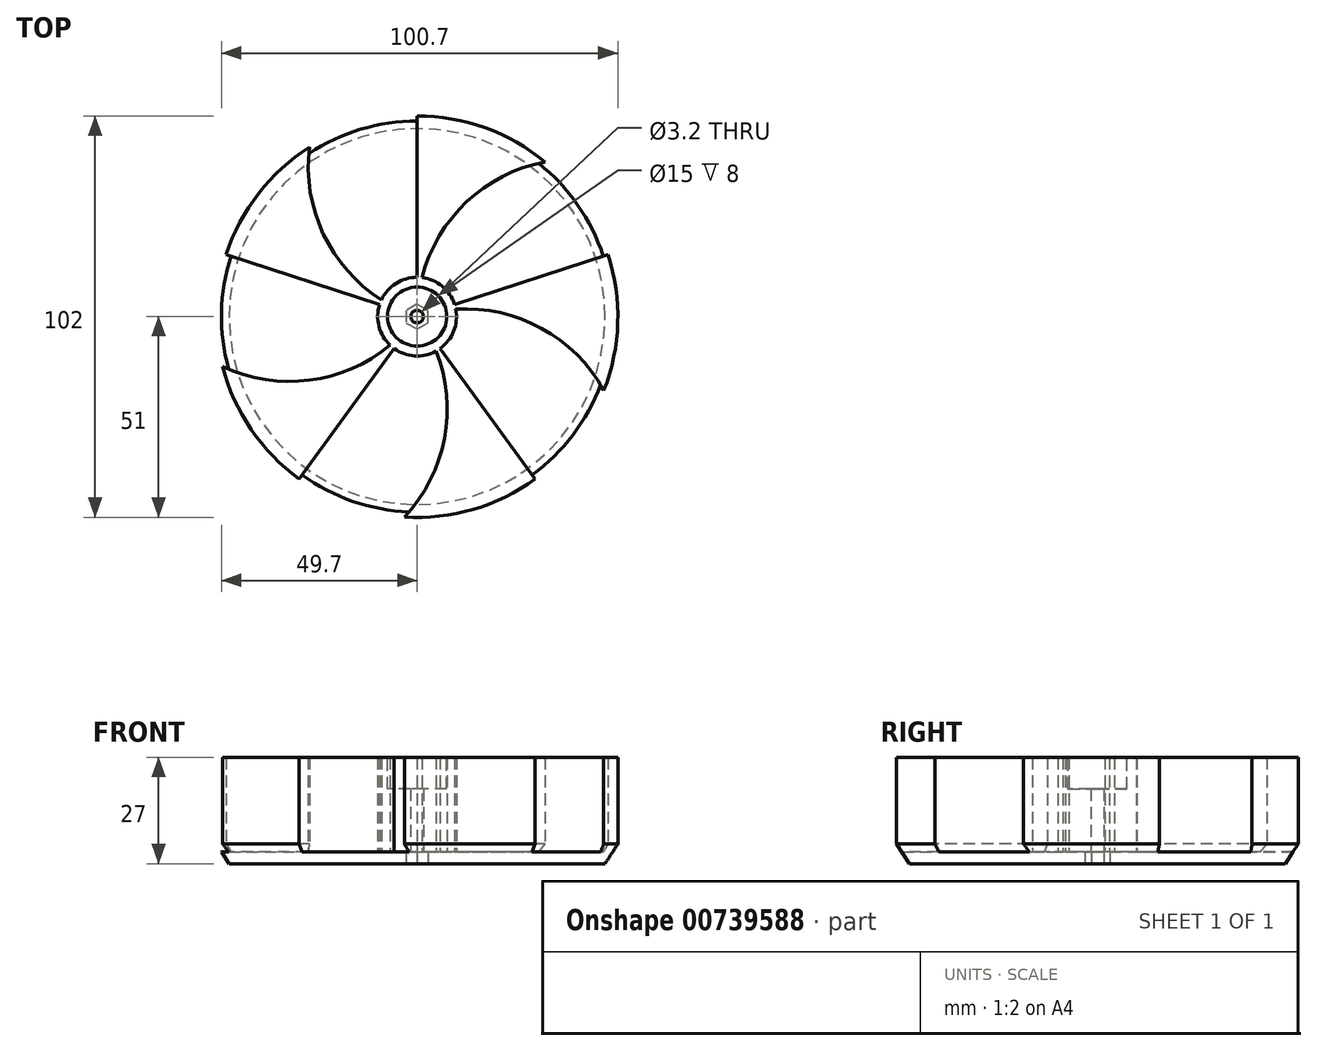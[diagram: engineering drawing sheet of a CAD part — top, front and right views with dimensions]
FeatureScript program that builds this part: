
annotation { "Feature Type Name" : "Feature", "Feature Type Description" : "" }
export const myFeature = defineFeature(function(context is Context, id is Id, definition is map)
    precondition{}
    {
        {
            var Q0;
            Q0=qCreatedBy(makeId("Top.planeOp"),FACE);
            var sketch = newSketch(context, id + "F0", { "sketchPlane" : qUnion([Q0])});
            skCircle(sketch, "E0", {"center": v(0, 0) * mm, "radius": 51 * mm});
            skSolve(sketch);
        }
        {
            var Q0;
            Q0 = qSketchRegion(id + "F0", true);
            extrude(context, id + "F1", {"entities" : qUnion([Q0]), "depth" : 3 * mm, "offsetDistance" : 25 * mm});
        }
        {
            var Q0;
            Q0=makeQuery(id+"F1.opExtrude","CAP_FACE",FACE,{"disambiguationData":[OSD([sQuery(id+"F0.wireOp",EDGE,"E0")])],"isStart":false});
            var sketch = newSketch(context, id + "F2", { "sketchPlane" : qUnion([Q0])});
            skLineSegment(sketch, "E1", {"start": v(0, 0) * mm, "end": v(0, 51) * mm});
            skArc(sketch, "E2", {"start": v(32.51, 39.3) * mm, "mid": v(9.18, 25.5) * mm, "end": v(0, 0) * mm});
            skLineSegment(sketch, "E3.1.0", {"start": v(0, 0) * mm, "end": v(-48.5, 15.76) * mm});
            skArc(sketch, "E3.1.1", {"start": v(-27.32, 43.06) * mm, "mid": v(-21.41, 16.61) * mm, "end": v(0, 0) * mm});
            skLineSegment(sketch, "E3.2.0", {"start": v(0, 0) * mm, "end": v(-29.98, -41.26) * mm});
            skArc(sketch, "E3.2.1", {"start": v(-49.4, -12.68) * mm, "mid": v(-22.42, -15.23) * mm, "end": v(0, 0) * mm});
            skLineSegment(sketch, "E3.3.0", {"start": v(0, 0) * mm, "end": v(29.98, -41.26) * mm});
            skArc(sketch, "E3.3.1", {"start": v(-3.2, -50.9) * mm, "mid": v(7.56, -26.03) * mm, "end": v(0, 0) * mm});
            skLineSegment(sketch, "E3.4.0", {"start": v(0, 0) * mm, "end": v(48.5, 15.76) * mm});
            skArc(sketch, "E3.4.1", {"start": v(47.42, -18.78) * mm, "mid": v(27.09, -0.85) * mm, "end": v(0, 0) * mm});
            skPoint(sketch, "E3.center", {"position": v(0, 0) * mm});
            skCircle(sketch, "E4", {"center": v(0, 0) * mm, "radius": 10 * mm});
            skSolve(sketch);
        }
        {
            var Q0;
            {var subQ0=sQuery(id+"F2.wireOp",EDGE,"E1");var subQ1=makeQuery(id+"F1.opExtrude","CAP_EDGE",EDGE,{"disambiguationData":[OSD([sQuery(id+"F0.wireOp",EDGE,"E0")])],"isStart":false});var subQ2=makeQuery(id+"F2.imprint","INTERSECT",VERTEX,{"derivedFrom":[subQ1,subQ0]});Q0=makeQuery(id+"F2.imprint","IMPRINT",FACE,{"disambiguationData":[TD([[makeQuery(id+"F2.imprint","IMPRINT",EDGE,{"disambiguationData":[TD([[subQ2,1.0]])],"derivedFrom":subQ0}),-1.0]])]});}
            var Q1;
            {var subQ0=sQuery(id+"F2.wireOp",EDGE,"E3.4.0");var subQ1=makeQuery(id+"F1.opExtrude","CAP_EDGE",EDGE,{"disambiguationData":[OSD([sQuery(id+"F0.wireOp",EDGE,"E0")])],"isStart":false});var subQ2=makeQuery(id+"F2.imprint","INTERSECT",VERTEX,{"derivedFrom":[subQ1,subQ0]});Q1=makeQuery(id+"F2.imprint","IMPRINT",FACE,{"disambiguationData":[TD([[makeQuery(id+"F2.imprint","IMPRINT",EDGE,{"disambiguationData":[TD([[subQ2,1.0]])],"derivedFrom":subQ0}),-1.0]])]});}
            var Q2;
            {var subQ0=sQuery(id+"F2.wireOp",EDGE,"E3.3.0");var subQ1=makeQuery(id+"F1.opExtrude","CAP_EDGE",EDGE,{"disambiguationData":[OSD([sQuery(id+"F0.wireOp",EDGE,"E0")])],"isStart":false});var subQ2=makeQuery(id+"F2.imprint","INTERSECT",VERTEX,{"derivedFrom":[subQ1,subQ0]});Q2=makeQuery(id+"F2.imprint","IMPRINT",FACE,{"disambiguationData":[TD([[makeQuery(id+"F2.imprint","IMPRINT",EDGE,{"disambiguationData":[TD([[subQ2,1.0]])],"derivedFrom":subQ0}),-1.0]])]});}
            var Q3;
            {var subQ0=sQuery(id+"F2.wireOp",EDGE,"E3.2.0");var subQ1=makeQuery(id+"F1.opExtrude","CAP_EDGE",EDGE,{"disambiguationData":[OSD([sQuery(id+"F0.wireOp",EDGE,"E0")])],"isStart":false});var subQ2=makeQuery(id+"F2.imprint","INTERSECT",VERTEX,{"derivedFrom":[subQ1,subQ0]});Q3=makeQuery(id+"F2.imprint","IMPRINT",FACE,{"disambiguationData":[TD([[makeQuery(id+"F2.imprint","IMPRINT",EDGE,{"disambiguationData":[TD([[subQ2,1.0]])],"derivedFrom":subQ0}),-1.0]])]});}
            var Q4;
            {var subQ0=sQuery(id+"F2.wireOp",EDGE,"E3.1.0");var subQ1=makeQuery(id+"F1.opExtrude","CAP_EDGE",EDGE,{"disambiguationData":[OSD([sQuery(id+"F0.wireOp",EDGE,"E0")])],"isStart":false});var subQ2=makeQuery(id+"F2.imprint","INTERSECT",VERTEX,{"derivedFrom":[subQ1,subQ0]});Q4=makeQuery(id+"F2.imprint","IMPRINT",FACE,{"disambiguationData":[TD([[makeQuery(id+"F2.imprint","IMPRINT",EDGE,{"disambiguationData":[TD([[subQ2,1.0]])],"derivedFrom":subQ0}),-1.0]])]});}
            var Q5;
            {var subQ1=sQuery(id+"F2.wireOp",EDGE,"E1");var subQ3=sQuery(id+"F2.wireOp",EDGE,"E4");var subQ4=makeQuery(id+"F2.imprint","INTERSECT",VERTEX,{"derivedFrom":[subQ1,subQ3]});Q5=makeQuery(id+"F2.imprint","IMPRINT",FACE,{"disambiguationData":[TD([[makeQuery(id+"F2.imprint","IMPRINT",EDGE,{"disambiguationData":[TD([[subQ4,-1.0]])],"derivedFrom":subQ3}),1.0]])]});}
            var Q6;
            {var subQ1=sQuery(id+"F2.wireOp",EDGE,"E3.1.0");var subQ3=sQuery(id+"F2.wireOp",EDGE,"E4");var subQ4=makeQuery(id+"F2.imprint","INTERSECT",VERTEX,{"derivedFrom":[subQ1,subQ3]});Q6=makeQuery(id+"F2.imprint","IMPRINT",FACE,{"disambiguationData":[TD([[makeQuery(id+"F2.imprint","IMPRINT",EDGE,{"disambiguationData":[TD([[subQ4,1.0]])],"derivedFrom":subQ3}),1.0]])]});}
            var Q7;
            {var subQ1=sQuery(id+"F2.wireOp",EDGE,"E3.1.0");var subQ3=sQuery(id+"F2.wireOp",EDGE,"E4");var subQ4=makeQuery(id+"F2.imprint","INTERSECT",VERTEX,{"derivedFrom":[subQ1,subQ3]});Q7=makeQuery(id+"F2.imprint","IMPRINT",FACE,{"disambiguationData":[TD([[makeQuery(id+"F2.imprint","IMPRINT",EDGE,{"disambiguationData":[TD([[subQ4,-1.0]])],"derivedFrom":subQ3}),1.0]])]});}
            var Q8;
            {var subQ1=sQuery(id+"F2.wireOp",EDGE,"E3.2.0");var subQ3=sQuery(id+"F2.wireOp",EDGE,"E4");var subQ4=makeQuery(id+"F2.imprint","INTERSECT",VERTEX,{"derivedFrom":[subQ1,subQ3]});Q8=makeQuery(id+"F2.imprint","IMPRINT",FACE,{"disambiguationData":[TD([[makeQuery(id+"F2.imprint","IMPRINT",EDGE,{"disambiguationData":[TD([[subQ4,-1.0]])],"derivedFrom":subQ3}),1.0]])]});}
            var Q9;
            {var subQ1=sQuery(id+"F2.wireOp",EDGE,"E3.2.0");var subQ3=sQuery(id+"F2.wireOp",EDGE,"E4");var subQ4=makeQuery(id+"F2.imprint","INTERSECT",VERTEX,{"derivedFrom":[subQ1,subQ3]});Q9=makeQuery(id+"F2.imprint","IMPRINT",FACE,{"disambiguationData":[TD([[makeQuery(id+"F2.imprint","IMPRINT",EDGE,{"disambiguationData":[TD([[subQ4,1.0]])],"derivedFrom":subQ3}),1.0]])]});}
            var Q10;
            {var subQ1=sQuery(id+"F2.wireOp",EDGE,"E3.3.0");var subQ3=sQuery(id+"F2.wireOp",EDGE,"E4");var subQ4=makeQuery(id+"F2.imprint","INTERSECT",VERTEX,{"derivedFrom":[subQ1,subQ3]});Q10=makeQuery(id+"F2.imprint","IMPRINT",FACE,{"disambiguationData":[TD([[makeQuery(id+"F2.imprint","IMPRINT",EDGE,{"disambiguationData":[TD([[subQ4,1.0]])],"derivedFrom":subQ3}),1.0]])]});}
            var Q11;
            {var subQ1=sQuery(id+"F2.wireOp",EDGE,"E3.3.0");var subQ3=sQuery(id+"F2.wireOp",EDGE,"E4");var subQ4=makeQuery(id+"F2.imprint","INTERSECT",VERTEX,{"derivedFrom":[subQ1,subQ3]});Q11=makeQuery(id+"F2.imprint","IMPRINT",FACE,{"disambiguationData":[TD([[makeQuery(id+"F2.imprint","IMPRINT",EDGE,{"disambiguationData":[TD([[subQ4,-1.0]])],"derivedFrom":subQ3}),1.0]])]});}
            var Q12;
            {var subQ1=sQuery(id+"F2.wireOp",EDGE,"E3.4.0");var subQ3=sQuery(id+"F2.wireOp",EDGE,"E4");var subQ4=makeQuery(id+"F2.imprint","INTERSECT",VERTEX,{"derivedFrom":[subQ1,subQ3]});Q12=makeQuery(id+"F2.imprint","IMPRINT",FACE,{"disambiguationData":[TD([[makeQuery(id+"F2.imprint","IMPRINT",EDGE,{"disambiguationData":[TD([[subQ4,1.0]])],"derivedFrom":subQ3}),1.0]])]});}
            var Q13;
            {var subQ1=sQuery(id+"F2.wireOp",EDGE,"E2");var subQ3=sQuery(id+"F2.wireOp",EDGE,"E4");var subQ4=makeQuery(id+"F2.imprint","INTERSECT",VERTEX,{"derivedFrom":[subQ1,subQ3]});Q13=makeQuery(id+"F2.imprint","IMPRINT",FACE,{"disambiguationData":[TD([[makeQuery(id+"F2.imprint","IMPRINT",EDGE,{"disambiguationData":[TD([[subQ4,1.0]])],"derivedFrom":subQ3}),1.0]])]});}
            var Q14;
            {var subQ1=sQuery(id+"F2.wireOp",EDGE,"E1");var subQ3=sQuery(id+"F2.wireOp",EDGE,"E4");var subQ4=makeQuery(id+"F2.imprint","INTERSECT",VERTEX,{"derivedFrom":[subQ1,subQ3]});Q14=makeQuery(id+"F2.imprint","IMPRINT",FACE,{"disambiguationData":[TD([[makeQuery(id+"F2.imprint","IMPRINT",EDGE,{"disambiguationData":[TD([[subQ4,1.0]])],"derivedFrom":subQ3}),1.0]])]});}
            extrude(context, id + "F3", {"entities" : qUnion([Q0, Q1, Q2, Q3, Q4, Q5, Q6, Q7, Q8, Q9, Q10, Q11, Q12, Q13, Q14]), "operationType" : NewBodyOperationType.ADD, "depth" : 24 * mm, "offsetDistance" : 25 * mm});
        }
        {
            var Q0;
            Q0=makeQuery(id+"F1.opExtrude","CAP_FACE",FACE,{"disambiguationData":[OSD([sQuery(id+"F0.wireOp",EDGE,"E0")])],"isStart":true});
            var sketch = newSketch(context, id + "F4", { "sketchPlane" : qUnion([Q0])});
            skCircle(sketch, "E5.cCircle", {"center": v(0, 0) * mm, "radius": 2.75 * mm, "construction": true});
            skLineSegment(sketch, "E5.0", {"start": v(2.75, 1.59) * mm, "end": v(2.75, -1.59) * mm});
            skLineSegment(sketch, "E5.1", {"start": v(2.75, -1.59) * mm, "end": v(0, -3.18) * mm});
            skLineSegment(sketch, "E5.2", {"start": v(0, -3.18) * mm, "end": v(-2.75, -1.59) * mm});
            skLineSegment(sketch, "E5.3", {"start": v(-2.75, -1.59) * mm, "end": v(-2.75, 1.59) * mm});
            skLineSegment(sketch, "E5.4", {"start": v(-2.75, 1.59) * mm, "end": v(0, 3.18) * mm});
            skLineSegment(sketch, "E5.5", {"start": v(0, 3.18) * mm, "end": v(2.75, 1.59) * mm});
            skPoint(sketch, "E5.0.midPoint", {"position": v(2.75, 0) * mm});
            skSolve(sketch);
        }
        {
            var Q0;
            Q0 = qSketchRegion(id + "F4", true);
            extrude(context, id + "F5", {"entities" : qUnion([Q0]), "operationType" : NewBodyOperationType.REMOVE, "oppositeDirection" : true, "depth" : 3 * mm, "offsetDistance" : 25 * mm});
        }
        {
            var Q0;
            Q0=makeQuery(id+"F5.boolean.opBoolean","COPY",FACE,{"derivedFrom":makeQuery(id+"F5.opExtrude","CAP_FACE",FACE,{"disambiguationData":[OSD([sQuery(id+"F4.wireOp",EDGE,"E5.0"),sQuery(id+"F4.wireOp",EDGE,"E5.1"),sQuery(id+"F4.wireOp",EDGE,"E5.2"),sQuery(id+"F4.wireOp",EDGE,"E5.3"),sQuery(id+"F4.wireOp",EDGE,"E5.4"),sQuery(id+"F4.wireOp",EDGE,"E5.5")])],"isStart":false})});
            var sketch = newSketch(context, id + "F6", { "sketchPlane" : qUnion([Q0])});
            skCircle(sketch, "E6", {"center": v(0, 0) * mm, "radius": 1.6 * mm});
            skSolve(sketch);
        }
        {
            var Q0;
            Q0=makeQuery(id+"F6.imprint","IMPRINT",FACE,{"disambiguationData":[TD([[makeQuery(id+"F6.imprint","IMPRINT",EDGE,{"derivedFrom":sQuery(id+"F6.wireOp",EDGE,"E6")}),1.0]])]});
            extrude(context, id + "F7", {"entities" : qUnion([Q0]), "operationType" : NewBodyOperationType.REMOVE, "endBound" : BoundingType.THROUGH_ALL, "oppositeDirection" : true, "depth" : 25 * mm, "offsetDistance" : 25 * mm});
        }
        {
            var Q0;
            Q0=makeQuery(id+"F3.opExtrude","CAP_FACE",FACE,{"disambiguationData":[OSD([sQuery(id+"F0.wireOp",EDGE,"E0"),sQuery(id+"F2.wireOp",EDGE,"E1"),sQuery(id+"F2.wireOp",EDGE,"E2"),sQuery(id+"F2.wireOp",EDGE,"E3.1.0"),sQuery(id+"F2.wireOp",EDGE,"E3.1.1"),sQuery(id+"F2.wireOp",EDGE,"E3.2.0"),sQuery(id+"F2.wireOp",EDGE,"E3.2.1"),sQuery(id+"F2.wireOp",EDGE,"E3.3.0"),sQuery(id+"F2.wireOp",EDGE,"E3.3.1"),sQuery(id+"F2.wireOp",EDGE,"E3.4.0"),sQuery(id+"F2.wireOp",EDGE,"E3.4.1"),sQuery(id+"F2.wireOp",EDGE,"E4")])],"isStart":false});
            var sketch = newSketch(context, id + "F8", { "sketchPlane" : qUnion([Q0])});
            skCircle(sketch, "E7", {"center": v(0, 0) * mm, "radius": 7.5 * mm});
            skSolve(sketch);
        }
        {
            var Q0;
            Q0 = qSketchRegion(id + "F8", true);
            extrude(context, id + "F9", {"entities" : qUnion([Q0]), "operationType" : NewBodyOperationType.REMOVE, "oppositeDirection" : true, "depth" : 8 * mm, "offsetDistance" : 25 * mm});
        }
        {
            var Q0;
            Q0=makeQuery(id+"F1.opExtrude","CAP_EDGE",EDGE,{"disambiguationData":[OSD([sQuery(id+"F0.wireOp",EDGE,"E0")])],"isStart":true});
            chamfer(context, id + "F10", {"entities" : qUnion([Q0]), "chamferType" : ChamferType.OFFSET_ANGLE, "width" : 5 * mm, "oppositeDirection" : false, "angle" : 33 * degree, "tangentPropagation" : true});
        }
    });
